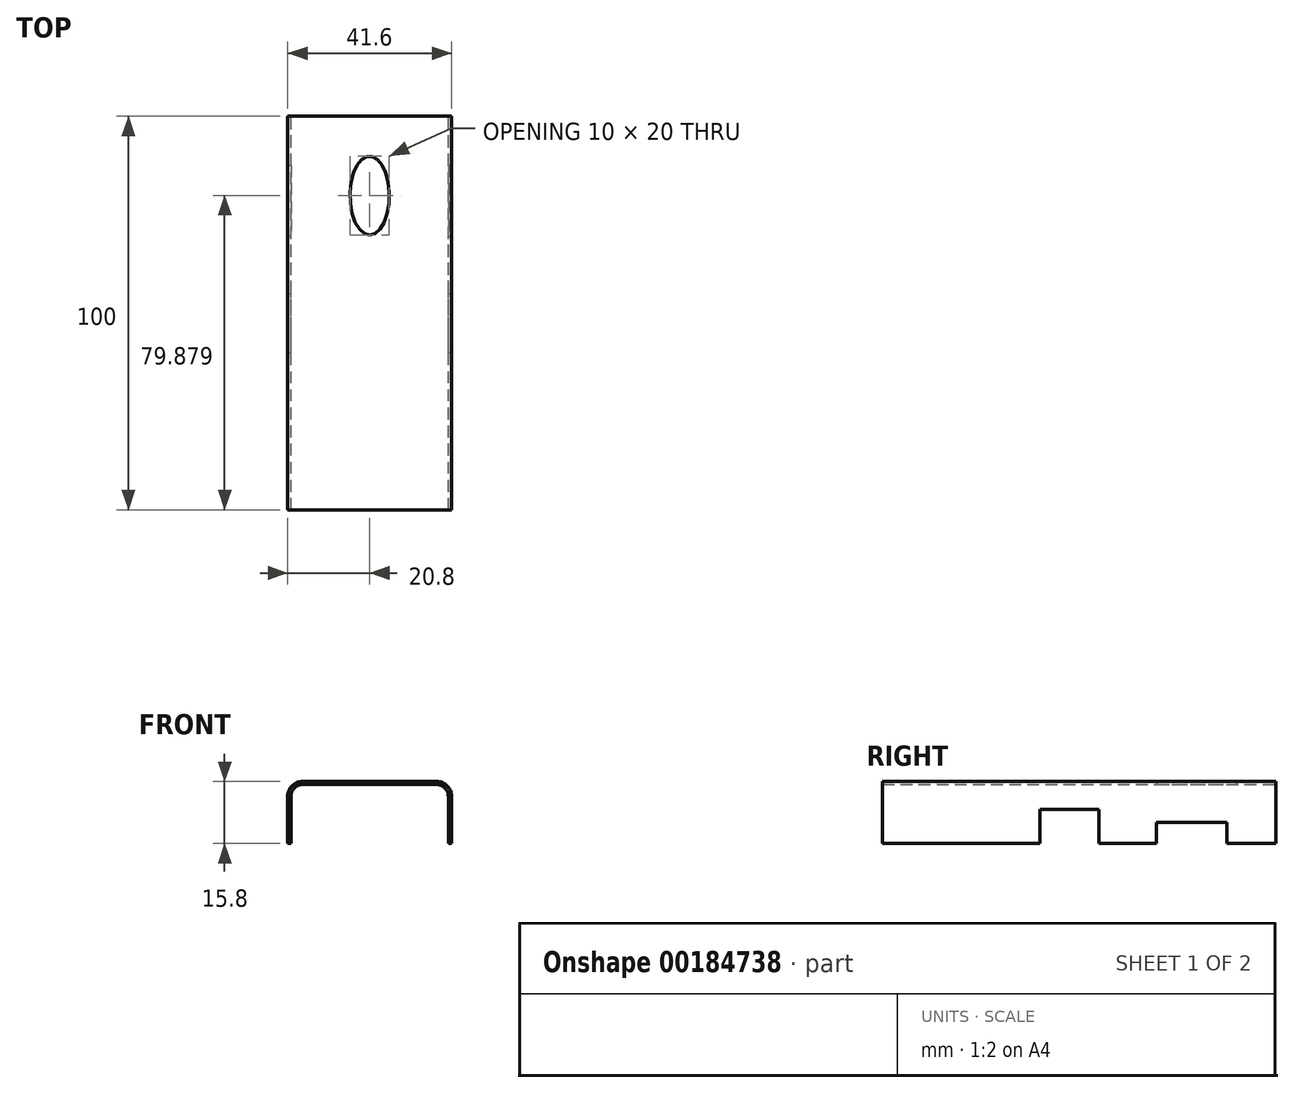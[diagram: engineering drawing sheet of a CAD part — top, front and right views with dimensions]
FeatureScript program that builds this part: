
annotation { "Feature Type Name" : "Feature", "Feature Type Description" : "" }
export const myFeature = defineFeature(function(context is Context, id is Id, definition is map)
    precondition{}
    {
        {
            var Q0;
            Q0=qCreatedBy(makeId("Front.planeOp"),FACE);
            var sketch = newSketch(context, id + "F0", { "sketchPlane" : qUnion([Q0])});
            skLineSegment(sketch, "E0", {"start": v(-20, 0) * mm, "end": v(20, 0) * mm, "construction": true});
            skLineSegment(sketch, "E1", {"start": v(-20, 0) * mm, "end": v(-20, 12) * mm});
            skLineSegment(sketch, "E2", {"start": v(-17, 15) * mm, "end": v(0, 15) * mm});
            skPoint(sketch, "E3.visualSharp", {"position": v(-20, 15) * mm});
            skArc(sketch, "E3.filletArc", {"start": v(-17, 15) * mm, "mid": v(-19.12, 14.12) * mm, "end": v(-20, 12) * mm});
            skLineSegment(sketch, "E4.MirrorCS", {"start": v(17, 15) * mm, "end": v(0, 15) * mm});
            skLineSegment(sketch, "E5.MirrorCS", {"start": v(20, 0) * mm, "end": v(20, 12) * mm});
            skArc(sketch, "E6.MirrorCS", {"start": v(17, 15) * mm, "mid": v(19.12, 14.12) * mm, "end": v(20, 12) * mm});
            skLineSegment(sketch, "E7.0", {"start": v(-17, 15.8) * mm, "end": v(-2.5, 15.8) * mm});
            skArc(sketch, "E7.1", {"start": v(-17, 15.8) * mm, "mid": v(-19.69, 14.69) * mm, "end": v(-20.8, 12) * mm});
            skLineSegment(sketch, "E7.2", {"start": v(-20.8, 0) * mm, "end": v(-20.8, 12) * mm});
            skLineSegment(sketch, "E8.MirrorCS", {"start": v(20.8, 0) * mm, "end": v(20.8, 12) * mm});
            skLineSegment(sketch, "E9.MirrorCS", {"start": v(17, 15.8) * mm, "end": v(2.5, 15.8) * mm});
            skArc(sketch, "E10.MirrorCS", {"start": v(17, 15.8) * mm, "mid": v(19.69, 14.69) * mm, "end": v(20.8, 12) * mm});
            skLineSegment(sketch, "E11", {"start": v(-20.8, 0) * mm, "end": v(-20, 0) * mm});
            skLineSegment(sketch, "E12", {"start": v(20.8, 0) * mm, "end": v(20, 0) * mm});
            skLineSegment(sketch, "E13", {"start": v(-2.5, 15.8) * mm, "end": v(2.5, 15.8) * mm});
            skSolve(sketch);
        }
        {
            var Q0;
            Q0=makeQuery(id+"F0.imprint","IMPRINT",FACE,{"disambiguationData":[TD([[makeQuery(id+"F0.imprint","IMPRINT",EDGE,{"derivedFrom":sQuery(id+"F0.wireOp",EDGE,"E1")}),1.0]])]});
            extrude(context, id + "F1", {"entities" : qUnion([Q0]), "depth" : 100 * mm});
        }
        {
            var Q0;
            Q0=makeQuery(id+"F1.opExtrude","SWEPT_FACE",FACE,{"disambiguationData":[OSD([sQuery(id+"F0.wireOp",EDGE,"E7.0"),sQuery(id+"F0.wireOp",EDGE,"E9.MirrorCS")])]});
            var sketch = newSketch(context, id + "F2", { "sketchPlane" : qUnion([Q0])});
            skEllipse(sketch, "E14", {"center": v(0, -20.12) * mm, "majorRadius": 10 * mm, "minorRadius": 5 * mm, "majorAxis": v(0, -1)});
            skSolve(sketch);
        }
        {
            var Q0;
            Q0=makeQuery(id+"F1.opExtrude","SWEPT_FACE",FACE,{"disambiguationData":[OSD([sQuery(id+"F0.wireOp",EDGE,"E8.MirrorCS")])]});
            var sketch = newSketch(context, id + "F3", { "sketchPlane" : qUnion([Q0])});
            skLineSegment(sketch, "E15.bottom", {"start": v(-45, 0) * mm, "end": v(-60, 0) * mm});
            skLineSegment(sketch, "E15.top", {"start": v(-45, 8.66) * mm, "end": v(-60, 8.66) * mm});
            skLineSegment(sketch, "E15.left", {"start": v(-45, 0) * mm, "end": v(-45, 8.66) * mm});
            skLineSegment(sketch, "E15.right", {"start": v(-60, 0) * mm, "end": v(-60, 8.66) * mm});
            skLineSegment(sketch, "E16.bottom", {"start": v(-30.42, 0) * mm, "end": v(-12.42, 0) * mm});
            skLineSegment(sketch, "E16.top", {"start": v(-30.42, 5.35) * mm, "end": v(-12.42, 5.35) * mm});
            skLineSegment(sketch, "E16.left", {"start": v(-30.42, 0) * mm, "end": v(-30.42, 5.35) * mm});
            skLineSegment(sketch, "E16.right", {"start": v(-12.42, 0) * mm, "end": v(-12.42, 5.35) * mm});
            skSolve(sketch);
        }
        {
            var Q0;
            Q0=makeQuery(id+"F3.imprint","IMPRINT",FACE,{"disambiguationData":[TD([[makeQuery(id+"F3.imprint","IMPRINT",EDGE,{"derivedFrom":sQuery(id+"F3.wireOp",EDGE,"E15.bottom")}),1.0]])]});
            var Q1;
            Q1=makeQuery(id+"F3.imprint","IMPRINT",FACE,{"disambiguationData":[TD([[makeQuery(id+"F3.imprint","IMPRINT",EDGE,{"derivedFrom":sQuery(id+"F3.wireOp",EDGE,"E16.bottom")}),1.0]])]});
            extrude(context, id + "F4", {"entities" : qUnion([Q0, Q1]), "operationType" : NewBodyOperationType.REMOVE, "endBound" : BoundingType.THROUGH_ALL, "oppositeDirection" : true, "depth" : 25 * mm});
        }
        {
            var Q0;
            Q0=makeQuery(id+"F2.imprint","IMPRINT",FACE,{"disambiguationData":[TD([[makeQuery(id+"F2.imprint","IMPRINT",EDGE,{"derivedFrom":sQuery(id+"F2.wireOp",EDGE,"E14")}),1.0]])]});
            extrude(context, id + "F5", {"entities" : qUnion([Q0]), "operationType" : NewBodyOperationType.REMOVE, "endBound" : BoundingType.THROUGH_ALL, "oppositeDirection" : true, "depth" : 25 * mm});
        }
    });
